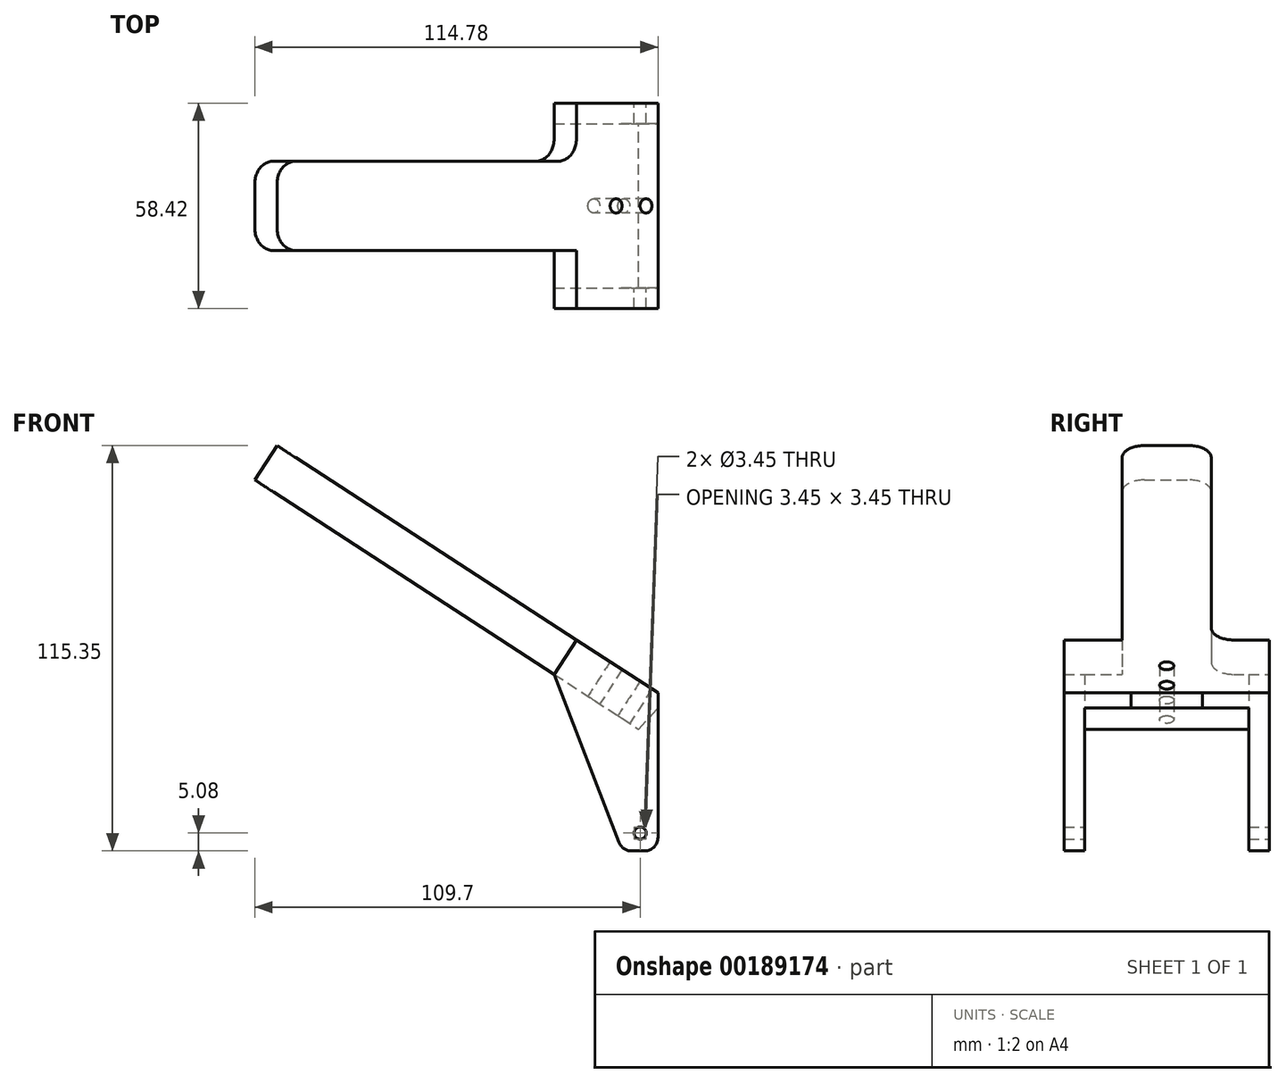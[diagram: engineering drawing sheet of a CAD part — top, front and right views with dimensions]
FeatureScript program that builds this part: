
annotation { "Feature Type Name" : "Feature", "Feature Type Description" : "" }
export const myFeature = defineFeature(function(context is Context, id is Id, definition is map)
    precondition{}
    {
        {
            var Q0;
            Q0=qCreatedBy(makeId("Front.planeOp"),FACE);
            var sketch = newSketch(context, id + "F0", { "sketchPlane" : qUnion([Q0])});
            skLineSegment(sketch, "E0", {"start": v(0, 0) * mm, "end": v(0, 29.21) * mm});
            skLineSegment(sketch, "E1", {"start": v(0, 0) * mm, "end": v(-10.16, 0) * mm});
            skLineSegment(sketch, "E2", {"start": v(-10.16, 0) * mm, "end": v(-10.16, 44.96) * mm});
            skLineSegment(sketch, "E3.0", {"start": v(0, 44.96) * mm, "end": v(12.7, 44.96) * mm});
            skLineSegment(sketch, "E4", {"start": v(0, 44.96) * mm, "end": v(0, 44.96) * mm});
            skLineSegment(sketch, "E5", {"start": v(0, 44.96) * mm, "end": v(-10.16, 44.96) * mm});
            skCircle(sketch, "E6", {"center": v(-5.08, 5.08) * mm, "radius": 1.73 * mm});
            skLineSegment(sketch, "E7", {"start": v(10.16, 39.88) * mm, "end": v(12.7, 44.96) * mm});
            skLineSegment(sketch, "E8", {"start": v(10.16, 39.88) * mm, "end": v(6.35, 39.88) * mm});
            skLineSegment(sketch, "E9", {"start": v(6.35, 39.88) * mm, "end": v(6.35, 41.8) * mm});
            skLineSegment(sketch, "E10", {"start": v(6.35, 41.8) * mm, "end": v(0, 41.8) * mm});
            skLineSegment(sketch, "E11", {"start": v(0, 41.8) * mm, "end": v(0, 29.21) * mm});
            skLineSegment(sketch, "E12", {"start": v(0, 44.96) * mm, "end": v(-23.22, 60.03) * mm});
            skLineSegment(sketch, "E13", {"start": v(-23.22, 60.03) * mm, "end": v(-29.56, 50.26) * mm});
            skLineSegment(sketch, "E14", {"start": v(-29.56, 50.26) * mm, "end": v(-10.16, 37.67) * mm});
            skSolve(sketch);
        }
        {
            var Q0;
            Q0=qSketchRegion(id+"F0",true);
            extrude(context, id + "F1", {"entities" : qUnion([Q0]), "endBound" : BoundingType.SYMMETRIC, "depth" : 58.42 * mm});
        }
        {
            var Q0;
            Q0=makeQuery(id+"F1.opExtrude","SWEPT_FACE",FACE,{"disambiguationData":[OSD([sQuery(id+"F0.wireOp",EDGE,"E0")])]});
            var sketch = newSketch(context, id + "F2", { "sketchPlane" : qUnion([Q0])});
            skLineSegment(sketch, "E15.bottom", {"start": v(23.37, 0) * mm, "end": v(-23.37, 0) * mm});
            skLineSegment(sketch, "E15.top", {"start": v(23.37, 40.64) * mm, "end": v(-23.37, 40.64) * mm});
            skLineSegment(sketch, "E15.left", {"start": v(23.37, 0) * mm, "end": v(23.37, 40.64) * mm});
            skLineSegment(sketch, "E15.right", {"start": v(-23.37, 0) * mm, "end": v(-23.37, 40.64) * mm});
            skSolve(sketch);
        }
        {
            var Q0;
            Q0=qSketchRegion(id+"F2",true);
            extrude(context, id + "F3", {"entities" : qUnion([Q0]), "operationType" : NewBodyOperationType.REMOVE, "oppositeDirection" : true, "depth" : 25.4 * mm});
        }
        {
            var Q0;
            Q0=makeQuery(id+"F1.opExtrude","CAP_FACE",FACE,{"disambiguationData":[OSD([sQuery(id+"F0.wireOp",EDGE,"E0"),sQuery(id+"F0.wireOp",EDGE,"E1"),sQuery(id+"F0.wireOp",EDGE,"E2"),sQuery(id+"F0.wireOp",EDGE,"prlR2u4p-7zGr-8wLY-PFS4-xYLywOnrNjr2"),sQuery(id+"F0.wireOp",EDGE,"E3.0"),sQuery(id+"F0.wireOp",EDGE,"42871ac2-c2a0-4b02-a882-5850723046cd"),sQuery(id+"F0.wireOp",EDGE,"E4"),sQuery(id+"F0.wireOp",EDGE,"E5"),sQuery(id+"F0.wireOp",EDGE,"RHK7HEwf-QzFp-As4H-Efqg-lgAJ1mc47Qq8"),sQuery(id+"F0.wireOp",EDGE,"HXlg5Q3d-pPcC-TzpV-dLrH-71LZfTlpnH6i"),sQuery(id+"F0.wireOp",EDGE,"39f0aba3-21ac-4e95-b7d3-faf603e52d2f"),sQuery(id+"F0.wireOp",EDGE,"E6")])],"isStart":true});
            var sketch = newSketch(context, id + "F4", { "sketchPlane" : qUnion([Q0])});
            skLineSegment(sketch, "E16.bottom", {"start": v(0, 38.6) * mm, "end": v(-15.24, 38.6) * mm});
            skLineSegment(sketch, "E16.top", {"start": v(0, 44.96) * mm, "end": v(-15.24, 44.96) * mm});
            skLineSegment(sketch, "E16.left", {"start": v(0, 38.6) * mm, "end": v(0, 44.96) * mm});
            skLineSegment(sketch, "E16.right", {"start": v(-15.24, 38.6) * mm, "end": v(-15.24, 44.96) * mm});
            skSolve(sketch);
        }
        {
            var Q0;
            Q0=qSketchRegion(id+"F4",true);
            extrude(context, id + "F5", {"entities" : qUnion([Q0]), "operationType" : NewBodyOperationType.REMOVE, "oppositeDirection" : true, "depth" : 19.05 * mm});
        }
        {
            var Q0;
            Q0=makeQuery(id+"F1.opExtrude","CAP_FACE",FACE,{"disambiguationData":[OSD([sQuery(id+"F0.wireOp",EDGE,"E0"),sQuery(id+"F0.wireOp",EDGE,"E1"),sQuery(id+"F0.wireOp",EDGE,"E2"),sQuery(id+"F0.wireOp",EDGE,"prlR2u4p-7zGr-8wLY-PFS4-xYLywOnrNjr2"),sQuery(id+"F0.wireOp",EDGE,"E3.0"),sQuery(id+"F0.wireOp",EDGE,"42871ac2-c2a0-4b02-a882-5850723046cd"),sQuery(id+"F0.wireOp",EDGE,"E5"),sQuery(id+"F0.wireOp",EDGE,"RHK7HEwf-QzFp-As4H-Efqg-lgAJ1mc47Qq8"),sQuery(id+"F0.wireOp",EDGE,"HXlg5Q3d-pPcC-TzpV-dLrH-71LZfTlpnH6i"),sQuery(id+"F0.wireOp",EDGE,"39f0aba3-21ac-4e95-b7d3-faf603e52d2f"),sQuery(id+"F0.wireOp",EDGE,"E6")])],"isStart":false});
            var sketch = newSketch(context, id + "F6", { "sketchPlane" : qUnion([Q0])});
            skLineSegment(sketch, "E17.bottom", {"start": v(0, 38.6) * mm, "end": v(15.24, 38.6) * mm});
            skLineSegment(sketch, "E17.top", {"start": v(0, 44.96) * mm, "end": v(15.24, 44.96) * mm});
            skLineSegment(sketch, "E17.left", {"start": v(0, 38.6) * mm, "end": v(0, 44.96) * mm});
            skLineSegment(sketch, "E17.right", {"start": v(15.24, 38.6) * mm, "end": v(15.24, 44.96) * mm});
            skSolve(sketch);
        }
        {
            var Q0;
            Q0=qSketchRegion(id+"F6",true);
            extrude(context, id + "F7", {"entities" : qUnion([Q0]), "operationType" : NewBodyOperationType.REMOVE, "oppositeDirection" : true, "depth" : 19.05 * mm});
        }
        {
            var Q0;
            Q0=makeQuery(id+"F7.boolean.opBoolean","COPY",FACE,{"derivedFrom":makeQuery(id+"F7.opExtrude","CAP_FACE",FACE,{"disambiguationData":[OSD([sQuery(id+"F6.wireOp",EDGE,"E17.bottom"),sQuery(id+"F6.wireOp",EDGE,"E17.top"),sQuery(id+"F6.wireOp",EDGE,"E17.left"),sQuery(id+"F6.wireOp",EDGE,"E17.right")])],"isStart":false})});
            var sketch = newSketch(context, id + "F8", { "sketchPlane" : qUnion([Q0])});
            skLineSegment(sketch, "E18", {"start": v(0, 41.8) * mm, "end": v(0, 40.64) * mm});
            skLineSegment(sketch, "E19", {"start": v(0, 40.64) * mm, "end": v(2.82, 41.8) * mm});
            skLineSegment(sketch, "E20", {"start": v(2.82, 41.8) * mm, "end": v(0, 41.8) * mm});
            skSolve(sketch);
        }
        {
            var Q0;
            Q0=qSketchRegion(id+"F8",true);
            extrude(context, id + "F9", {"entities" : qUnion([Q0]), "operationType" : NewBodyOperationType.ADD, "oppositeDirection" : true, "depth" : 20.32 * mm});
        }
        {
            var Q0;
            Q0=qCreatedBy(makeId("Front.planeOp"),FACE);
            var sketch = newSketch(context, id + "F10", { "sketchPlane" : qUnion([Q0])});
            skLineSegment(sketch, "E21", {"start": v(12.7, 44.96) * mm, "end": v(0, 44.96) * mm});
            skLineSegment(sketch, "E22", {"start": v(12.7, 44.96) * mm, "end": v(-13.18, 61.76) * mm});
            skLineSegment(sketch, "E23", {"start": v(-16.95, 55.96) * mm, "end": v(0, 44.96) * mm});
            skLineSegment(sketch, "E24", {"start": v(-16.95, 55.96) * mm, "end": v(-13.18, 61.76) * mm});
            skSolve(sketch);
        }
        {
            var Q0;
            Q0=qSketchRegion(id+"F10",true);
            extrude(context, id + "F11", {"entities" : qUnion([Q0]), "operationType" : NewBodyOperationType.ADD, "endBound" : BoundingType.SYMMETRIC, "depth" : 20.32 * mm});
        }
        {
            var Q0;
            Q0=makeQuery(id+"F1.opExtrude","SWEPT_EDGE",EDGE,{"disambiguationData":[OSD([sQuery(id+"F0.wireOp",EDGE,"E8"),sQuery(id+"F0.wireOp",EDGE,"E9")])]});
            chamfer(context, id + "F12", {"entities" : qUnion([Q0]), "chamferType" : ChamferType.OFFSET_ANGLE, "width" : 1.27 * mm, "oppositeDirection" : false, "angle" : 33 * degree, "tangentPropagation" : true});
        }
        {
            var Q0;
            Q0=makeQuery(id+"F1.opExtrude","SWEPT_FACE",FACE,{"disambiguationData":[OSD([sQuery(id+"F0.wireOp",EDGE,"E13")])]});
            var sketch = newSketch(context, id + "F13", { "sketchPlane" : qUnion([Q0])});
            skLineSegment(sketch, "E25.bottom", {"start": v(-12.7, 37.71) * mm, "end": v(12.7, 37.71) * mm});
            skLineSegment(sketch, "E25.top", {"start": v(-12.7, 26.06) * mm, "end": v(12.7, 26.06) * mm});
            skLineSegment(sketch, "E25.left", {"start": v(-12.7, 37.71) * mm, "end": v(-12.7, 26.06) * mm});
            skLineSegment(sketch, "E25.right", {"start": v(12.7, 37.71) * mm, "end": v(12.7, 26.06) * mm});
            skSolve(sketch);
        }
        {
            var Q0;
            Q0=qSketchRegion(id+"F13",true);
            extrude(context, id + "F14", {"entities" : qUnion([Q0]), "operationType" : NewBodyOperationType.ADD, "depth" : 101.6 * mm});
        }
        {
            var Q0;
            Q0=makeQuery(id+"F11.opExtrude","SWEPT_EDGE",EDGE,{"disambiguationData":[OSD([sQuery(id+"F10.wireOp",EDGE,"E22"),sQuery(id+"F10.wireOp",EDGE,"E24")])]});
            fillet(context, id + "F15", {"entities" : qUnion([Q0]), "radius" : 2.54 * mm, "tangentPropagation" : true, "allowEdgeOverflow" : false});
        }
        {
            var Q0;
            Q0=makeQuery(id+"F14.opExtrude","CAP_EDGE",EDGE,{"disambiguationData":[OSD([sQuery(id+"F13.wireOp",EDGE,"E25.right")])],"isStart":true});
            var Q1;
            Q1=makeQuery(id+"F14.opExtrude","CAP_EDGE",EDGE,{"disambiguationData":[OSD([sQuery(id+"F13.wireOp",EDGE,"E25.left")])],"isStart":true});
            var Q2;
            Q2=makeQuery(id+"F14.opExtrude","CAP_EDGE",EDGE,{"disambiguationData":[OSD([sQuery(id+"F13.wireOp",EDGE,"E25.left")])],"isStart":false});
            var Q3;
            Q3=makeQuery(id+"F14.opExtrude","CAP_EDGE",EDGE,{"disambiguationData":[OSD([sQuery(id+"F13.wireOp",EDGE,"E25.right")])],"isStart":false});
            fillet(context, id + "F16", {"entities" : qUnion([Q0, Q1, Q2, Q3]), "radius" : 6.35 * mm, "tangentPropagation" : true, "allowEdgeOverflow" : false});
        }
        {
            var Q0;
            Q0=makeQuery(id+"F1.opExtrude","SWEPT_EDGE",EDGE,{"disambiguationData":[OSD([sQuery(id+"F0.wireOp",EDGE,"E9"),sQuery(id+"F0.wireOp",EDGE,"E10")])]});
            fillet(context, id + "F17", {"entities" : qUnion([Q0]), "radius" : 0.8 * mm, "tangentPropagation" : true, "allowEdgeOverflow" : false});
        }
        {
            var Q0;
            Q0=makeQuery(id+"F1.opExtrude","CAP_FACE",FACE,{"disambiguationData":[OSD([sQuery(id+"F0.wireOp",EDGE,"E0"),sQuery(id+"F0.wireOp",EDGE,"E1"),sQuery(id+"F0.wireOp",EDGE,"E2"),sQuery(id+"F0.wireOp",EDGE,"E3.0"),sQuery(id+"F0.wireOp",EDGE,"E6"),sQuery(id+"F0.wireOp",EDGE,"E7"),sQuery(id+"F0.wireOp",EDGE,"E8"),sQuery(id+"F0.wireOp",EDGE,"E9"),sQuery(id+"F0.wireOp",EDGE,"E10"),sQuery(id+"F0.wireOp",EDGE,"E11"),sQuery(id+"F0.wireOp",EDGE,"E12"),sQuery(id+"F0.wireOp",EDGE,"E13"),sQuery(id+"F0.wireOp",EDGE,"E14")])],"isStart":false});
            var sketch = newSketch(context, id + "F18", { "sketchPlane" : qUnion([Q0])});
            skLineSegment(sketch, "E26", {"start": v(-29.56, 50.26) * mm, "end": v(-10.16, 0) * mm});
            skSolve(sketch);
        }
        {
            var Q0;
            Q0=qSketchRegion(id+"F18",true);
            var Q1;
            Q1=makeQuery(id+"F18.imprint","IMPRINT",FACE,{"disambiguationData":[TD([[makeQuery(id+"F18.imprint","IMPRINT",EDGE,{"derivedFrom":sQuery(id+"F18.wireOp",EDGE,"E26")}),1.0]])]});
            extrude(context, id + "F19", {"entities" : qUnion([Q0, Q1]), "operationType" : NewBodyOperationType.ADD, "oppositeDirection" : true, "depth" : 5.84 * mm});
        }
        {
            var Q0;
            Q0=makeQuery(id+"F1.opExtrude","CAP_FACE",FACE,{"disambiguationData":[OSD([sQuery(id+"F0.wireOp",EDGE,"E0"),sQuery(id+"F0.wireOp",EDGE,"E1"),sQuery(id+"F0.wireOp",EDGE,"E2"),sQuery(id+"F0.wireOp",EDGE,"E3.0"),sQuery(id+"F0.wireOp",EDGE,"E6"),sQuery(id+"F0.wireOp",EDGE,"E7"),sQuery(id+"F0.wireOp",EDGE,"E8"),sQuery(id+"F0.wireOp",EDGE,"E9"),sQuery(id+"F0.wireOp",EDGE,"E10"),sQuery(id+"F0.wireOp",EDGE,"E11"),sQuery(id+"F0.wireOp",EDGE,"E12"),sQuery(id+"F0.wireOp",EDGE,"E13"),sQuery(id+"F0.wireOp",EDGE,"E14")])],"isStart":true});
            var sketch = newSketch(context, id + "F20", { "sketchPlane" : qUnion([Q0])});
            skLineSegment(sketch, "E27", {"start": v(29.56, 50.26) * mm, "end": v(10.16, 0) * mm});
            skSolve(sketch);
        }
        {
            var Q0;
            Q0=makeQuery(id+"F20.imprint","IMPRINT",FACE,{"disambiguationData":[TD([[makeQuery(id+"F20.imprint","IMPRINT",EDGE,{"derivedFrom":sQuery(id+"F20.wireOp",EDGE,"E27")}),-1.0]])]});
            extrude(context, id + "F21", {"entities" : qUnion([Q0]), "operationType" : NewBodyOperationType.ADD, "oppositeDirection" : true, "depth" : 5.84 * mm});
        }
        {
            var Q0;
            {var subQ0=sQuery(id+"F0.wireOp",EDGE,"E0");var subQ1=sQuery(id+"F0.wireOp",EDGE,"E1");Q0=makeQuery(id+"F3.boolean.opBoolean","SPLIT",EDGE,{"disambiguationData":[TD([makeQuery(id+"F3.opExtrude","SWEPT_FACE",FACE,{"disambiguationData":[OSD([sQuery(id+"F2.wireOp",EDGE,"E15.right")])]})])],"derivedFrom":makeQuery(id+"F1.opExtrude","SWEPT_EDGE",EDGE,{"disambiguationData":[OSD([subQ0,subQ1])]})});}
            var Q1;
            {var subQ0=sQuery(id+"F0.wireOp",EDGE,"E0");var subQ1=sQuery(id+"F0.wireOp",EDGE,"E1");Q1=makeQuery(id+"F3.boolean.opBoolean","SPLIT",EDGE,{"disambiguationData":[TD([makeQuery(id+"F3.opExtrude","SWEPT_FACE",FACE,{"disambiguationData":[OSD([sQuery(id+"F2.wireOp",EDGE,"E15.left")])]})])],"derivedFrom":makeQuery(id+"F1.opExtrude","SWEPT_EDGE",EDGE,{"disambiguationData":[OSD([subQ0,subQ1])]})});}
            var Q2;
            {var subQ0=sQuery(id+"F0.wireOp",EDGE,"E2");var subQ1=sQuery(id+"F0.wireOp",EDGE,"E1");Q2=makeQuery(id+"F3.boolean.opBoolean","SPLIT",EDGE,{"disambiguationData":[TD([makeQuery(id+"F3.opExtrude","SWEPT_FACE",FACE,{"disambiguationData":[OSD([sQuery(id+"F2.wireOp",EDGE,"E15.right")])]})])],"derivedFrom":makeQuery(id+"F1.opExtrude","SWEPT_EDGE",EDGE,{"disambiguationData":[OSD([subQ1,subQ0])]})});}
            var Q3;
            {var subQ0=sQuery(id+"F0.wireOp",EDGE,"E2");var subQ1=sQuery(id+"F0.wireOp",EDGE,"E1");Q3=makeQuery(id+"F3.boolean.opBoolean","SPLIT",EDGE,{"disambiguationData":[TD([makeQuery(id+"F3.opExtrude","SWEPT_FACE",FACE,{"disambiguationData":[OSD([sQuery(id+"F2.wireOp",EDGE,"E15.left")])]})])],"derivedFrom":makeQuery(id+"F1.opExtrude","SWEPT_EDGE",EDGE,{"disambiguationData":[OSD([subQ1,subQ0])]})});}
            fillet(context, id + "F22", {"entities" : qUnion([Q0, Q1, Q2, Q3]), "radius" : 3.8 * mm, "tangentPropagation" : true, "allowEdgeOverflow" : false});
        }
        {
            var Q0;
            Q0=makeQuery(id+"F11.boolean.opBoolean","MERGE",FACE,{"derivedFrom":[makeQuery(id+"F9.boolean.opBoolean","MERGE",FACE,{"derivedFrom":[makeQuery(id+"F7.boolean.opBoolean","COPY",FACE,{"derivedFrom":makeQuery(id+"F7.opExtrude","CAP_FACE",FACE,{"disambiguationData":[OSD([sQuery(id+"F6.wireOp",EDGE,"E17.bottom"),sQuery(id+"F6.wireOp",EDGE,"E17.top"),sQuery(id+"F6.wireOp",EDGE,"E17.left"),sQuery(id+"F6.wireOp",EDGE,"E17.right")])],"isStart":false})}),makeQuery(id+"F9.opExtrude","CAP_FACE",FACE,{"disambiguationData":[OSD([sQuery(id+"F8.wireOp",EDGE,"E18"),sQuery(id+"F8.wireOp",EDGE,"E19"),sQuery(id+"F8.wireOp",EDGE,"E20")])],"isStart":true})]}),makeQuery(id+"F11.opExtrude","CAP_FACE",FACE,{"disambiguationData":[OSD([sQuery(id+"F10.wireOp",EDGE,"E21"),sQuery(id+"F10.wireOp",EDGE,"E22"),sQuery(id+"F10.wireOp",EDGE,"E23"),sQuery(id+"F10.wireOp",EDGE,"E24")])],"isStart":false})]});
            var sketch = newSketch(context, id + "F23", { "sketchPlane" : qUnion([Q0])});
            skLineSegment(sketch, "E28", {"start": v(-16.95, 55.96) * mm, "end": v(0, 44.96) * mm});
            skLineSegment(sketch, "E29", {"start": v(0, 44.96) * mm, "end": v(0, 37.8) * mm});
            skLineSegment(sketch, "E30", {"start": v(0, 37.8) * mm, "end": v(17.36, 37.8) * mm});
            skLineSegment(sketch, "E31", {"start": v(17.36, 37.8) * mm, "end": v(17.36, 44.8) * mm});
            skLineSegment(sketch, "E32", {"start": v(17.36, 44.8) * mm, "end": v(-12.28, 63.15) * mm});
            skLineSegment(sketch, "E33", {"start": v(-16.95, 55.96) * mm, "end": v(-12.28, 63.15) * mm});
            skSolve(sketch);
        }
        {
            var Q0;
            {var subQ11=sQuery(id+"F23.wireOp",EDGE,"E30");Q0=makeQuery(id+"F23.imprint","IMPRINT",FACE,{"disambiguationData":[TD([[makeQuery(id+"F23.imprint","IMPRINT",EDGE,{"derivedFrom":subQ11}),1.0]])]});}
            var Q1;
            {var subQ13=sQuery(id+"F23.wireOp",EDGE,"E28");Q1=makeQuery(id+"F23.imprint","IMPRINT",FACE,{"disambiguationData":[TD([[makeQuery(id+"F23.imprint","IMPRINT",EDGE,{"derivedFrom":subQ13}),1.0]])]});}
            extrude(context, id + "F24", {"entities" : qUnion([Q0, Q1]), "operationType" : NewBodyOperationType.REMOVE, "oppositeDirection" : true, "depth" : 25.4 * mm});
        }
        {
            var Q0;
            Q0=makeQuery(id+"F21.boolean.opBoolean","MERGE",FACE,{"derivedFrom":[makeQuery(id+"F3.boolean.opBoolean","COPY",FACE,{"derivedFrom":makeQuery(id+"F3.opExtrude","SWEPT_FACE",FACE,{"disambiguationData":[OSD([sQuery(id+"F2.wireOp",EDGE,"E15.left")])]})}),makeQuery(id+"F21.opExtrude","CAP_FACE",FACE,{"disambiguationData":[OSD([sQuery(id+"F0.wireOp",EDGE,"E2"),sQuery(id+"F0.wireOp",EDGE,"E14"),sQuery(id+"F20.wireOp",EDGE,"E27")])],"isStart":false})]});
            var sketch = newSketch(context, id + "F25", { "sketchPlane" : qUnion([Q0])});
            skLineSegment(sketch, "E34", {"start": v(-14.74, 40.64) * mm, "end": v(-5.48, 34.63) * mm});
            skLineSegment(sketch, "E35", {"start": v(-5.48, 34.63) * mm, "end": v(0, 40.64) * mm});
            skLineSegment(sketch, "E36", {"start": v(0, 40.64) * mm, "end": v(-14.74, 40.64) * mm});
            skSolve(sketch);
        }
        {
            var Q0;
            Q0=makeQuery(id+"F25.imprint","IMPRINT",FACE,{"disambiguationData":[TD([[makeQuery(id+"F25.imprint","IMPRINT",EDGE,{"derivedFrom":sQuery(id+"F25.wireOp",EDGE,"E34")}),1.0]])]});
            extrude(context, id + "F26", {"entities" : qUnion([Q0]), "operationType" : NewBodyOperationType.ADD, "depth" : 46.74 * mm});
        }
        {
            var Q0;
            Q0=makeQuery(id+"F26.boolean.opBoolean","MERGE",FACE,{"derivedFrom":[makeQuery(id+"F14.boolean.opBoolean","MERGE",FACE,{"derivedFrom":[makeQuery(id+"F1.opExtrude","SWEPT_FACE",FACE,{"disambiguationData":[OSD([sQuery(id+"F0.wireOp",EDGE,"E14")])]}),makeQuery(id+"F14.opExtrude","SWEPT_FACE",FACE,{"disambiguationData":[OSD([sQuery(id+"F13.wireOp",EDGE,"E25.top")])]})]}),makeQuery(id+"F26.opExtrude","SWEPT_FACE",FACE,{"disambiguationData":[OSD([sQuery(id+"F25.wireOp",EDGE,"E34")])]})]});
            var sketch = newSketch(context, id + "F27", { "sketchPlane" : qUnion([Q0])});
            skCircle(sketch, "E37", {"center": v(-28.53, 0) * mm, "radius": 2.03 * mm});
            skCircle(sketch, "E38", {"center": v(-38.7, 0) * mm, "radius": 2.03 * mm});
            skSolve(sketch);
        }
        {
            var Q0;
            Q0=makeQuery(id+"F27.imprint","IMPRINT",FACE,{"disambiguationData":[TD([[makeQuery(id+"F27.imprint","IMPRINT",EDGE,{"derivedFrom":sQuery(id+"F27.wireOp",EDGE,"E37")}),1.0]])]});
            var Q1;
            Q1=makeQuery(id+"F27.imprint","IMPRINT",FACE,{"disambiguationData":[TD([[makeQuery(id+"F27.imprint","IMPRINT",EDGE,{"derivedFrom":sQuery(id+"F27.wireOp",EDGE,"E38")}),1.0]])]});
            extrude(context, id + "F28", {"entities" : qUnion([Q0, Q1]), "operationType" : NewBodyOperationType.REMOVE, "endBound" : BoundingType.THROUGH_ALL, "oppositeDirection" : true, "depth" : 25.4 * mm});
        }
    });
